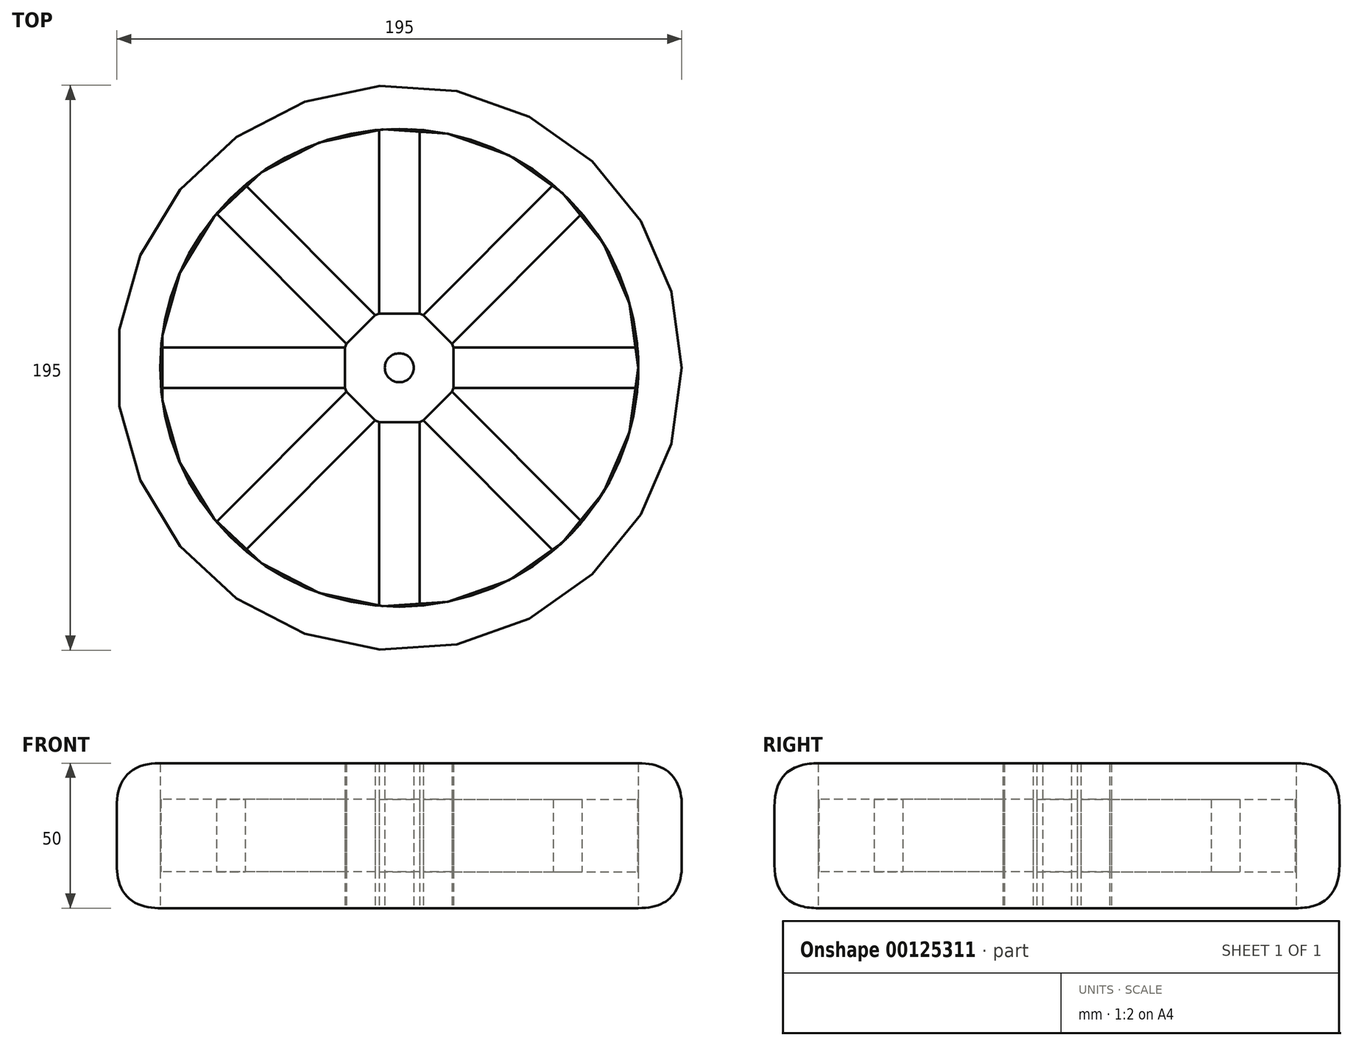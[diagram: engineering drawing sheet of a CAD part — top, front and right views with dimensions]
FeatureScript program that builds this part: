
annotation { "Feature Type Name" : "Feature", "Feature Type Description" : "" }
export const myFeature = defineFeature(function(context is Context, id is Id, definition is map)
    precondition{}
    {
        {
            var Q0;
            Q0=qCreatedBy(makeId("Top.planeOp"),FACE);
            var sketch = newSketch(context, id + "F0", { "sketchPlane" : qUnion([Q0])});
            skCircle(sketch, "E0", {"center": v(0, 0) * mm, "radius": 97.5 * mm});
            skCircle(sketch, "E1", {"center": v(0, 0) * mm, "radius": 5 * mm});
            skCircle(sketch, "E2", {"center": v(0, 0) * mm, "radius": 82.5 * mm});
            skPoint(sketch, "E3.center", {"position": v(0.16, 0.16) * mm});
            skLineSegment(sketch, "E4", {"start": v(0, 0) * mm, "end": v(0, 82.5) * mm});
            skLineSegment(sketch, "E5", {"start": v(-7, 18.73) * mm, "end": v(-7, 82.2) * mm});
            skLineSegment(sketch, "E6", {"start": v(7, 18.73) * mm, "end": v(7, 82.2) * mm});
            skLineSegment(sketch, "E7", {"start": v(-7, 18.73) * mm, "end": v(7, 18.73) * mm});
            skLineSegment(sketch, "E8.1.0", {"start": v(-18.2, 8.3) * mm, "end": v(-63.08, 53.18) * mm});
            skLineSegment(sketch, "E8.1.1", {"start": v(-18.2, 8.3) * mm, "end": v(-8.3, 18.2) * mm});
            skLineSegment(sketch, "E8.1.2", {"start": v(-8.3, 18.2) * mm, "end": v(-53.18, 63.08) * mm});
            skLineSegment(sketch, "E8.2.0", {"start": v(-18.73, -7) * mm, "end": v(-82.2, -7) * mm});
            skLineSegment(sketch, "E8.2.1", {"start": v(-18.73, -7) * mm, "end": v(-18.73, 7) * mm});
            skLineSegment(sketch, "E8.2.2", {"start": v(-18.73, 7) * mm, "end": v(-82.2, 7) * mm});
            skLineSegment(sketch, "E8.3.0", {"start": v(-8.3, -18.2) * mm, "end": v(-53.18, -63.08) * mm});
            skLineSegment(sketch, "E8.3.1", {"start": v(-8.3, -18.2) * mm, "end": v(-18.2, -8.3) * mm});
            skLineSegment(sketch, "E8.3.2", {"start": v(-18.2, -8.3) * mm, "end": v(-63.08, -53.18) * mm});
            skLineSegment(sketch, "E8.4.0", {"start": v(7, -18.73) * mm, "end": v(7, -82.2) * mm});
            skLineSegment(sketch, "E8.4.1", {"start": v(7, -18.73) * mm, "end": v(-7, -18.73) * mm});
            skLineSegment(sketch, "E8.4.2", {"start": v(-7, -18.73) * mm, "end": v(-7, -82.2) * mm});
            skLineSegment(sketch, "E8.5.0", {"start": v(18.2, -8.3) * mm, "end": v(63.08, -53.18) * mm});
            skLineSegment(sketch, "E8.5.1", {"start": v(18.2, -8.3) * mm, "end": v(8.3, -18.2) * mm});
            skLineSegment(sketch, "E8.5.2", {"start": v(8.3, -18.2) * mm, "end": v(53.18, -63.08) * mm});
            skLineSegment(sketch, "E8.6.0", {"start": v(18.73, 7) * mm, "end": v(82.2, 7) * mm});
            skLineSegment(sketch, "E8.6.1", {"start": v(18.73, 7) * mm, "end": v(18.73, -7) * mm});
            skLineSegment(sketch, "E8.6.2", {"start": v(18.73, -7) * mm, "end": v(82.2, -7) * mm});
            skLineSegment(sketch, "E8.7.0", {"start": v(8.3, 18.2) * mm, "end": v(53.18, 63.08) * mm});
            skLineSegment(sketch, "E8.7.1", {"start": v(8.3, 18.2) * mm, "end": v(18.2, 8.3) * mm});
            skLineSegment(sketch, "E8.7.2", {"start": v(18.2, 8.3) * mm, "end": v(63.08, 53.18) * mm});
            skLineSegment(sketch, "E9", {"start": v(-8.3, 18.2) * mm, "end": v(-7, 18.73) * mm});
            skLineSegment(sketch, "E10", {"start": v(7, 18.73) * mm, "end": v(8.3, 18.2) * mm});
            skLineSegment(sketch, "E11", {"start": v(18.73, -7) * mm, "end": v(18.2, -8.3) * mm});
            skLineSegment(sketch, "E12", {"start": v(8.3, -18.2) * mm, "end": v(7, -18.73) * mm});
            skLineSegment(sketch, "E13", {"start": v(-7, -18.73) * mm, "end": v(-8.3, -18.2) * mm});
            skLineSegment(sketch, "E14", {"start": v(-18.73, -7) * mm, "end": v(-18.2, -8.3) * mm});
            skLineSegment(sketch, "E15", {"start": v(-18.73, 7) * mm, "end": v(-18.2, 8.3) * mm});
            skLineSegment(sketch, "E16", {"start": v(18.2, 8.3) * mm, "end": v(18.73, 7) * mm});
            skSolve(sketch);
        }
        {
            var Q0;
            Q0=makeQuery(id+"F0.imprint","IMPRINT",FACE,{"disambiguationData":[TD([[makeQuery(id+"F0.imprint","IMPRINT",EDGE,{"derivedFrom":sQuery(id+"F0.wireOp",EDGE,"E0")}),1.0]])]});
            var Q1;
            Q1=makeQuery(id+"F0.imprint","IMPRINT",FACE,{"disambiguationData":[TD([[makeQuery(id+"F0.imprint","IMPRINT",EDGE,{"derivedFrom":sQuery(id+"F0.wireOp",EDGE,"E1")}),-1.0]])]});
            extrude(context, id + "F1", {"entities" : qUnion([Q0, Q1]), "endBound" : BoundingType.SYMMETRIC, "depth" : 50 * mm});
        }
        {
            var Q0;
            {var subQ0=sQuery(id+"F0.wireOp",EDGE,"E8.1.0");Q0=makeQuery(id+"F0.imprint","IMPRINT",FACE,{"disambiguationData":[TD([[makeQuery(id+"F0.imprint","IMPRINT",EDGE,{"derivedFrom":subQ0}),-1.0]])]});}
            var Q1;
            {var subQ3=sQuery(id+"F0.wireOp",EDGE,"E5");Q1=makeQuery(id+"F0.imprint","IMPRINT",FACE,{"disambiguationData":[TD([[makeQuery(id+"F0.imprint","IMPRINT",EDGE,{"derivedFrom":subQ3}),-1.0]])]});}
            var Q2;
            {var subQ3=sQuery(id+"F0.wireOp",EDGE,"E6");Q2=makeQuery(id+"F0.imprint","IMPRINT",FACE,{"disambiguationData":[TD([[makeQuery(id+"F0.imprint","IMPRINT",EDGE,{"derivedFrom":subQ3}),1.0]])]});}
            var Q3;
            {var subQ0=sQuery(id+"F0.wireOp",EDGE,"E8.7.0");Q3=makeQuery(id+"F0.imprint","IMPRINT",FACE,{"disambiguationData":[TD([[makeQuery(id+"F0.imprint","IMPRINT",EDGE,{"derivedFrom":subQ0}),-1.0]])]});}
            var Q4;
            {var subQ0=sQuery(id+"F0.wireOp",EDGE,"E8.6.0");Q4=makeQuery(id+"F0.imprint","IMPRINT",FACE,{"disambiguationData":[TD([[makeQuery(id+"F0.imprint","IMPRINT",EDGE,{"derivedFrom":subQ0}),-1.0]])]});}
            var Q5;
            {var subQ0=sQuery(id+"F0.wireOp",EDGE,"E8.5.0");Q5=makeQuery(id+"F0.imprint","IMPRINT",FACE,{"disambiguationData":[TD([[makeQuery(id+"F0.imprint","IMPRINT",EDGE,{"derivedFrom":subQ0}),-1.0]])]});}
            var Q6;
            {var subQ0=sQuery(id+"F0.wireOp",EDGE,"E8.4.0");Q6=makeQuery(id+"F0.imprint","IMPRINT",FACE,{"disambiguationData":[TD([[makeQuery(id+"F0.imprint","IMPRINT",EDGE,{"derivedFrom":subQ0}),-1.0]])]});}
            var Q7;
            {var subQ0=sQuery(id+"F0.wireOp",EDGE,"E8.3.0");Q7=makeQuery(id+"F0.imprint","IMPRINT",FACE,{"disambiguationData":[TD([[makeQuery(id+"F0.imprint","IMPRINT",EDGE,{"derivedFrom":subQ0}),-1.0]])]});}
            var Q8;
            {var subQ0=sQuery(id+"F0.wireOp",EDGE,"E8.2.0");Q8=makeQuery(id+"F0.imprint","IMPRINT",FACE,{"disambiguationData":[TD([[makeQuery(id+"F0.imprint","IMPRINT",EDGE,{"derivedFrom":subQ0}),-1.0]])]});}
            extrude(context, id + "F2", {"entities" : qUnion([Q0, Q1, Q2, Q3, Q4, Q5, Q6, Q7, Q8]), "endBound" : BoundingType.SYMMETRIC, "depth" : 25 * mm});
        }
        {
            var Q0;
            Q0=makeQuery(id+"F1.opExtrude","SWEPT_FACE",FACE,{"disambiguationData":[OSD([sQuery(id+"F0.wireOp",EDGE,"E0")])]});
            fillet(context, id + "F3", {"entities" : qUnion([Q0]), "radius" : 15 * mm, "tangentPropagation" : true, "rho" : 0.5, "crossSection" : FilletCrossSection.CONIC, "allowEdgeOverflow" : false});
        }
    });
